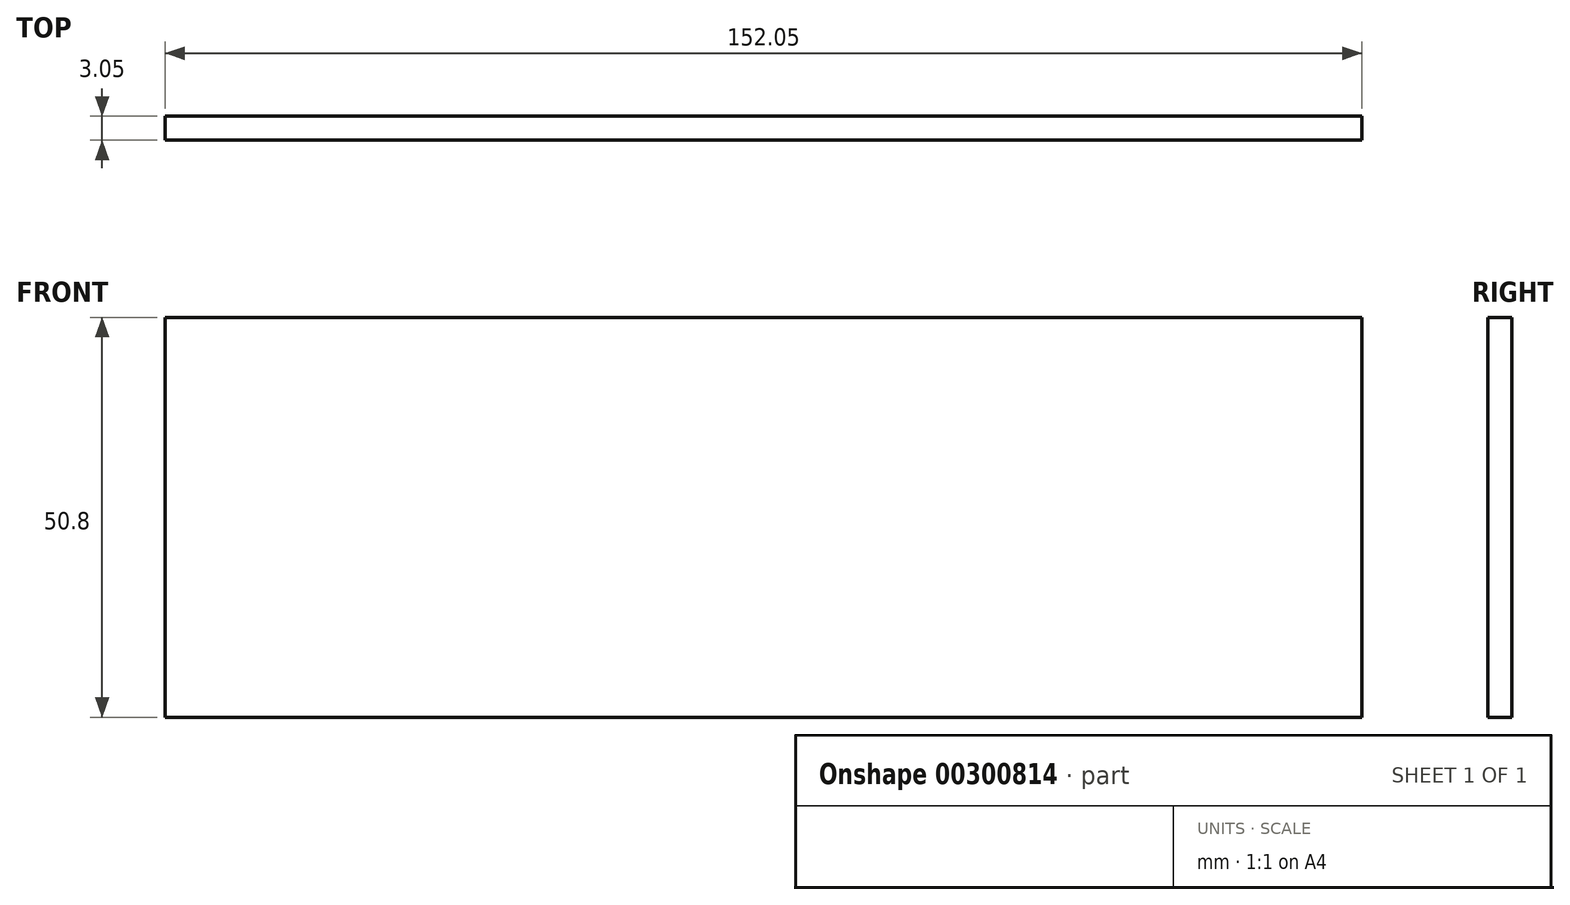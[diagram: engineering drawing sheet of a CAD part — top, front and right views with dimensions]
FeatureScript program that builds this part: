
annotation { "Feature Type Name" : "Feature", "Feature Type Description" : "" }
export const myFeature = defineFeature(function(context is Context, id is Id, definition is map)
    precondition{}
    {
        {
            var Q0;
            Q0=qCreatedBy(makeId("Front.planeOp"),FACE);
            var sketch = newSketch(context, id + "F0", { "sketchPlane" : qUnion([Q0])});
            skLineSegment(sketch, "E0.bottom", {"start": v(-107.64, 50.8) * mm, "end": v(44.4, 50.8) * mm});
            skLineSegment(sketch, "E0.top", {"start": v(-107.64, 0) * mm, "end": v(44.4, 0) * mm});
            skLineSegment(sketch, "E0.left", {"start": v(-107.64, 50.8) * mm, "end": v(-107.64, 0) * mm});
            skLineSegment(sketch, "E0.right", {"start": v(44.4, 50.8) * mm, "end": v(44.4, 0) * mm});
            skSolve(sketch);
        }
        {
            var Q0;
            Q0 = qSketchRegion(id + "F0", true);
            extrude(context, id + "F1", {"entities" : qUnion([Q0]), "oppositeDirection" : true, "depth" : 3.05 * mm});
        }
    });
